# Revit family: Shower-Shower_Door-KOHLER-SKYLINE-K-22319T
name_source: partatom
category: Specialty Equipment
revit_build: Autodesk Revit 2017 (Build: 20160225_1515(x64)
units: mm (PartAtom-declared; Revit-internal decimal feet)

## family parameters
Cut with Voids When Loaded = No
Host = Face
OmniClass Number = 23.31.17.17
OmniClass Title = Shower Enclosures
Part Type = Normal
Room Calculation Point = No
Round Connector Dimension = Use Diameter
Shared = No

## types (3) — shared parameters
ADA Compliant = No
Assembly Code = C1030200
Date Modified = 08/30/2020
Default Elevation = 0"
Description = Sliding shower screen 2 door 2 panel, 10mm glass thickness
Height = 78 3/4"
Length = 5 1/4"
Manufacturer = KOHLER Co.
Master Format 2014 = 10 28 19.16
Master Format 2014 Name = Shower Doors
Material = Premium Metal Construction
Product Name = SKYLINE
URL = http://www.kohler.com.cn
WaterSense Certified = No
Width = 94 7/16"

## per-type parameters (varying)
| type | Finish | Model | Type |
| AF-Flange Gold | Kohler-Metal-AF-Flange_Gold | K-22319T-FM-AF | 1 |
| RGD-Rose Gold | Kohler-Metal-RGD-Rose_Gold | K-22319T-FM-RGD | 2 |
| S-Bright Silver | Kohler-Metal-S-Stainless_Steel | K-22319T-FM-S | 3 |

## geometry (parser evidence)
native form markers: Sweep x4
no freeform markers — native parametric forms only
